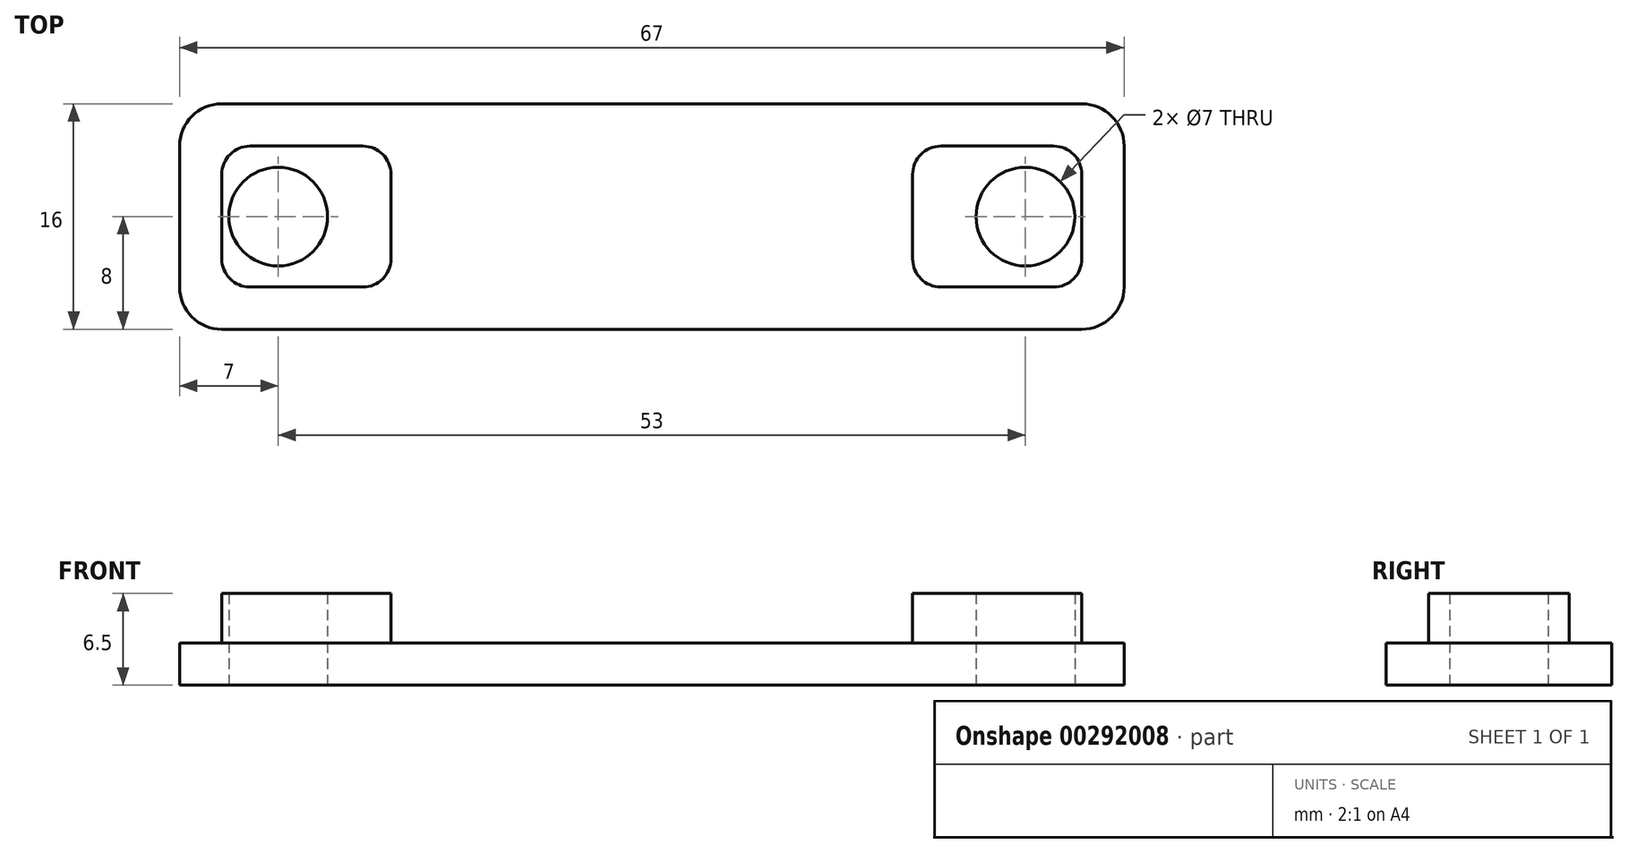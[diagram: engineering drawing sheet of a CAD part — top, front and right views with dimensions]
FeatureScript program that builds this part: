
annotation { "Feature Type Name" : "Feature", "Feature Type Description" : "" }
export const myFeature = defineFeature(function(context is Context, id is Id, definition is map)
    precondition{}
    {
        {
            var Q0;
            Q0=qCreatedBy(makeId("Top.planeOp"),FACE);
            var sketch = newSketch(context, id + "F0", { "sketchPlane" : qUnion([Q0])});
            skLineSegment(sketch, "E0.bottom", {"start": v(33.5, -8) * mm, "end": v(-33.5, -8) * mm});
            skLineSegment(sketch, "E0.top", {"start": v(33.5, 8) * mm, "end": v(-33.5, 8) * mm});
            skLineSegment(sketch, "E0.left", {"start": v(33.5, -8) * mm, "end": v(33.5, 8) * mm});
            skLineSegment(sketch, "E0.right", {"start": v(-33.5, -8) * mm, "end": v(-33.5, 8) * mm});
            skPoint(sketch, "E0.middle", {"position": v(0, 0) * mm});
            skCircle(sketch, "E1", {"center": v(26.5, 0) * mm, "radius": 3.5 * mm});
            skCircle(sketch, "E2", {"center": v(-26.5, 0) * mm, "radius": 3.5 * mm});
            skSolve(sketch);
        }
        {
            var Q0;
            Q0 = qSketchRegion(id + "F0", true);
            extrude(context, id + "F1", {"entities" : qUnion([Q0]), "depth" : 3 * mm});
        }
        {
            var Q0;
            Q0=makeQuery(id+"F1.opExtrude","CAP_FACE",FACE,{"disambiguationData":[OSD([sQuery(id+"F0.wireOp",EDGE,"E0.bottom"),sQuery(id+"F0.wireOp",EDGE,"E0.top"),sQuery(id+"F0.wireOp",EDGE,"E0.left"),sQuery(id+"F0.wireOp",EDGE,"E0.right"),sQuery(id+"F0.wireOp",EDGE,"E1"),sQuery(id+"F0.wireOp",EDGE,"E2")])],"isStart":false});
            var sketch = newSketch(context, id + "F2", { "sketchPlane" : qUnion([Q0])});
            skLineSegment(sketch, "E3.bottom", {"start": v(28.5, -5) * mm, "end": v(20.5, -5) * mm});
            skLineSegment(sketch, "E3.top", {"start": v(28.5, 5) * mm, "end": v(20.5, 5) * mm});
            skLineSegment(sketch, "E3.left", {"start": v(30.5, -3) * mm, "end": v(30.5, 3) * mm});
            skLineSegment(sketch, "E3.right", {"start": v(18.5, -3) * mm, "end": v(18.5, 3) * mm});
            skPoint(sketch, "E3.middle", {"position": v(24.5, 0) * mm});
            skLineSegment(sketch, "E4.bottom", {"start": v(-20.5, -5) * mm, "end": v(-28.5, -5) * mm});
            skLineSegment(sketch, "E4.top", {"start": v(-20.5, 5) * mm, "end": v(-28.5, 5) * mm});
            skLineSegment(sketch, "E4.left", {"start": v(-18.5, -3) * mm, "end": v(-18.5, 3) * mm});
            skLineSegment(sketch, "E4.right", {"start": v(-30.5, -3) * mm, "end": v(-30.5, 3) * mm});
            skPoint(sketch, "E4.middle", {"position": v(-24.5, 0) * mm});
            skPoint(sketch, "E5.visualSharp", {"position": v(-30.5, 5) * mm});
            skArc(sketch, "E5.filletArc", {"start": v(-28.5, 5) * mm, "mid": v(-29.91, 4.41) * mm, "end": v(-30.5, 3) * mm});
            skPoint(sketch, "E6.visualSharp", {"position": v(-18.5, 5) * mm});
            skArc(sketch, "E6.filletArc", {"start": v(-18.5, 3) * mm, "mid": v(-19.09, 4.41) * mm, "end": v(-20.5, 5) * mm});
            skPoint(sketch, "E7.visualSharp", {"position": v(-18.5, -5) * mm});
            skArc(sketch, "E7.filletArc", {"start": v(-20.5, -5) * mm, "mid": v(-19.09, -4.41) * mm, "end": v(-18.5, -3) * mm});
            skPoint(sketch, "E8.visualSharp", {"position": v(-30.5, -5) * mm});
            skArc(sketch, "E8.filletArc", {"start": v(-30.5, -3) * mm, "mid": v(-29.91, -4.41) * mm, "end": v(-28.5, -5) * mm});
            skPoint(sketch, "E9.visualSharp", {"position": v(18.5, -5) * mm});
            skArc(sketch, "E9.filletArc", {"start": v(18.5, -3) * mm, "mid": v(19.09, -4.41) * mm, "end": v(20.5, -5) * mm});
            skPoint(sketch, "E10.visualSharp", {"position": v(18.5, 5) * mm});
            skArc(sketch, "E10.filletArc", {"start": v(20.5, 5) * mm, "mid": v(19.09, 4.41) * mm, "end": v(18.5, 3) * mm});
            skPoint(sketch, "E11.visualSharp", {"position": v(30.5, 5) * mm});
            skArc(sketch, "E11.filletArc", {"start": v(30.5, 3) * mm, "mid": v(29.91, 4.41) * mm, "end": v(28.5, 5) * mm});
            skPoint(sketch, "E12.visualSharp", {"position": v(30.5, -5) * mm});
            skArc(sketch, "E12.filletArc", {"start": v(28.5, -5) * mm, "mid": v(29.91, -4.41) * mm, "end": v(30.5, -3) * mm});
            skSolve(sketch);
        }
        {
            var Q0;
            Q0 = qSketchRegion(id + "F2", true);
            extrude(context, id + "F3", {"entities" : qUnion([Q0]), "operationType" : NewBodyOperationType.ADD, "depth" : 3.5 * mm});
        }
        {
            var Q0;
            Q0=makeQuery(id+"F3.opExtrude","CAP_FACE",FACE,{"disambiguationData":[OSD([sQuery(id+"F2.wireOp",EDGE,"E4.bottom"),sQuery(id+"F2.wireOp",EDGE,"E4.top"),sQuery(id+"F2.wireOp",EDGE,"E4.left"),sQuery(id+"F2.wireOp",EDGE,"E4.right"),sQuery(id+"F2.wireOp",EDGE,"E5.filletArc"),sQuery(id+"F2.wireOp",EDGE,"E6.filletArc"),sQuery(id+"F2.wireOp",EDGE,"E7.filletArc"),sQuery(id+"F2.wireOp",EDGE,"E8.filletArc")])],"isStart":false});
            var sketch = newSketch(context, id + "F4", { "sketchPlane" : qUnion([Q0])});
            skCircle(sketch, "E13", {"center": v(26.5, 0) * mm, "radius": 3.5 * mm});
            skCircle(sketch, "E14", {"center": v(-26.5, 0) * mm, "radius": 3.5 * mm});
            skSolve(sketch);
        }
        {
            var Q0;
            Q0 = qSketchRegion(id + "F4", true);
            extrude(context, id + "F5", {"entities" : qUnion([Q0]), "operationType" : NewBodyOperationType.REMOVE, "endBound" : BoundingType.THROUGH_ALL, "oppositeDirection" : true, "depth" : 25 * mm});
        }
        {
            var Q0;
            Q0=makeQuery(id+"F1.opExtrude","SWEPT_EDGE",EDGE,{"disambiguationData":[OSD([sQuery(id+"F0.wireOp",EDGE,"E0.top"),sQuery(id+"F0.wireOp",EDGE,"E0.right")])]});
            var Q1;
            Q1=makeQuery(id+"F1.opExtrude","SWEPT_EDGE",EDGE,{"disambiguationData":[OSD([sQuery(id+"F0.wireOp",EDGE,"E0.top"),sQuery(id+"F0.wireOp",EDGE,"E0.left")])]});
            var Q2;
            Q2=makeQuery(id+"F1.opExtrude","SWEPT_EDGE",EDGE,{"disambiguationData":[OSD([sQuery(id+"F0.wireOp",EDGE,"E0.bottom"),sQuery(id+"F0.wireOp",EDGE,"E0.left")])]});
            var Q3;
            Q3=makeQuery(id+"F1.opExtrude","SWEPT_EDGE",EDGE,{"disambiguationData":[OSD([sQuery(id+"F0.wireOp",EDGE,"E0.bottom"),sQuery(id+"F0.wireOp",EDGE,"E0.right")])]});
            fillet(context, id + "F6", {"entities" : qUnion([Q0, Q1, Q2, Q3]), "radius" : 3 * mm, "tangentPropagation" : true, "allowEdgeOverflow" : false});
        }
    });
